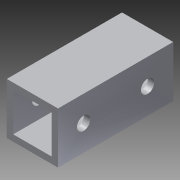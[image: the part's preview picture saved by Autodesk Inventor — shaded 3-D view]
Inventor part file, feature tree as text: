
AUTODESK INVENTOR PART (.ipt)
format: ipt  version: 2013 (Build 170138000, 138)  size: 96,256 bytes
history: native  units: in
note: dims shown in document units (in); Inventor stores cm internally (conversion verified against a paired STEP export)
features: extrude x2, sketch x2
ambient origin geometry x8: Origin, YZ Plane, XZ Plane, XY Plane, X Axis, Y Axis, Z Axis, Center Point
bodies: Solid1 (feature_tree)
feature tree (4):
  extrude  "Extrusion1"  Depth=1.0in
  extrude  "Extrusion2"  Depth=2.25in TaperAngle=0.0deg
  sketch  "Sketch1"  dims[d0=1.0in d1=1.0in]
  sketch  "Sketch2"  dims[d2=0.125in d3=2.25in d4=0.0in d5=1.25in d7=0.5in d8=0.26in d9=2.25in d10=0.0in]
